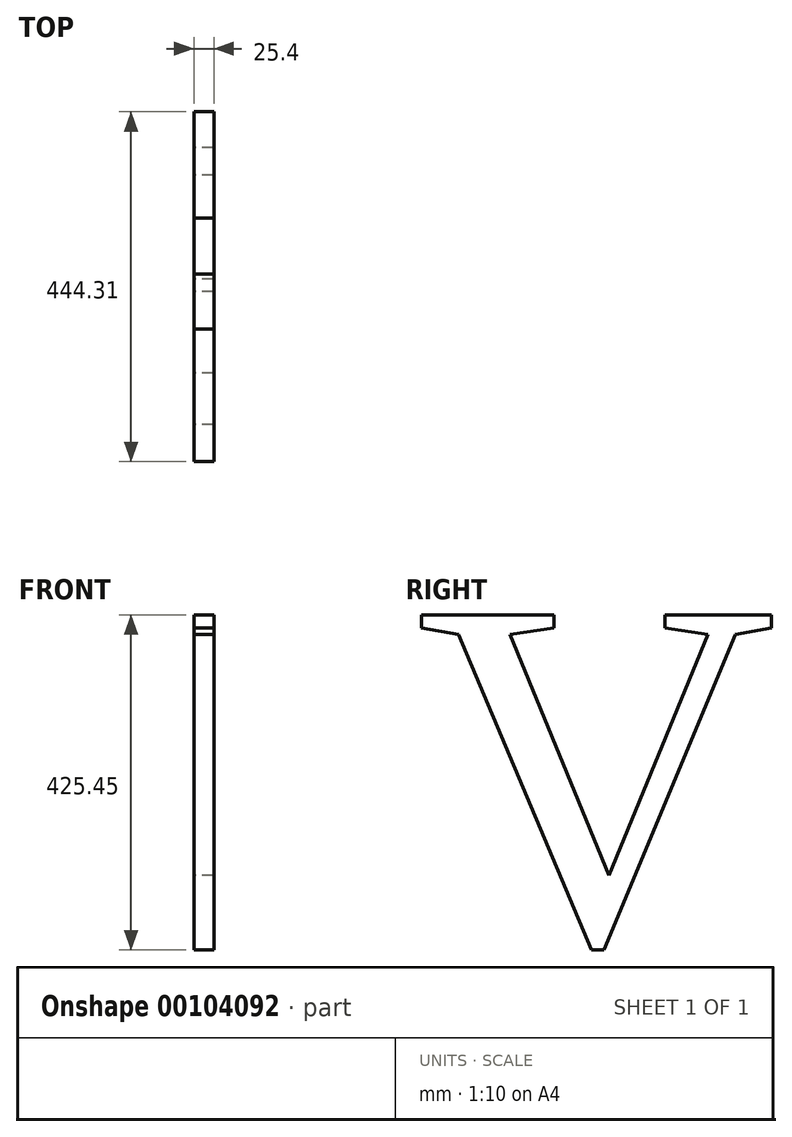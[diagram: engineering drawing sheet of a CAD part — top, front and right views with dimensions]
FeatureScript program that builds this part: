
annotation { "Feature Type Name" : "Feature", "Feature Type Description" : "" }
export const myFeature = defineFeature(function(context is Context, id is Id, definition is map)
    precondition{}
    {
        {
            var Q0;
            Q0=qCreatedBy(makeId("Right.planeOp"),FACE);
            var sketch = newSketch(context, id + "F0", { "sketchPlane" : qUnion([Q0])});
            skText(sketch, "E0", { "text": "V", "fontName": "Tinos-Regular.ttf"});
            const initialGuessF0  = {"E0": [-0.45145, 0, 1, 0, 0.4572]};
            skSetInitialGuess(sketch, initialGuessF0);
            skSolve(sketch);
        }
        {
            var Q0;
            Q0 = qSketchRegion(id + "F0", true);
            extrude(context, id + "F1", {"entities" : qUnion([Q0]), "depth" : 25.4 * mm});
        }
    });
